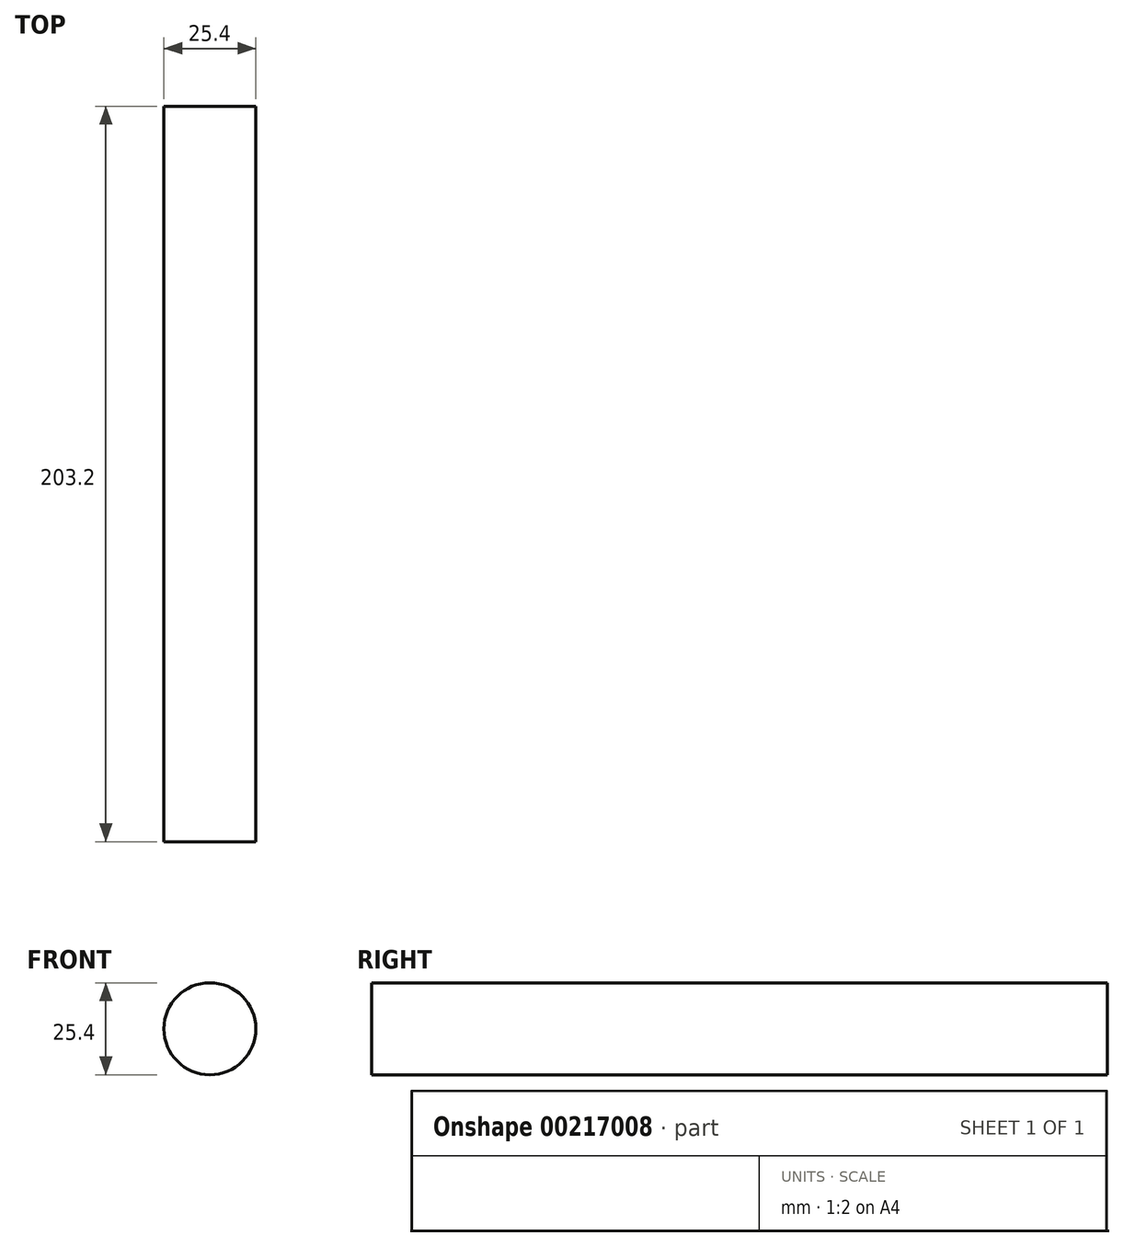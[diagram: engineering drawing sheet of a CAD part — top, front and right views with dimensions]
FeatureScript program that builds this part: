
annotation { "Feature Type Name" : "Feature", "Feature Type Description" : "" }
export const myFeature = defineFeature(function(context is Context, id is Id, definition is map)
    precondition{}
    {
        {
            var Q0;
            Q0=qCreatedBy(makeId("Front.planeOp"),FACE);
            var sketch = newSketch(context, id + "F0", { "sketchPlane" : qUnion([Q0])});
            skCircle(sketch, "E0", {"center": v(0, 0) * mm, "radius": 12.7 * mm});
            skSolve(sketch);
        }
        {
            var Q0;
            Q0=makeQuery(id+"F0.imprint","IMPRINT",FACE,{"disambiguationData":[TD([[makeQuery(id+"F0.imprint","IMPRINT",EDGE,{"derivedFrom":sQuery(id+"F0.wireOp",EDGE,"E0")}),1.0]])]});
            extrude(context, id + "F1", {"entities" : qUnion([Q0]), "depth" : 203.2 * mm});
        }
    });
